# Revit family: Access_Door_ACUDOR_High-Security_SD-6000
name_source: partatom
category: Doors
revit_build: Autodesk Revit 2017 (Build: 20171027_0315(x64)
units: mm (PartAtom-declared; Revit-internal decimal feet)

## family parameters
Cut with Voids When Loaded = No
Host = Face
Room Calculation Point = No
Shared = No

## types (6) — shared parameters
Analytic Construction = <None>
Default Elevation = 48 "
Description = HIGH-SECURITY
Manufacturer = ACUDOR
Material Finish = Metal - Acudor - Stainless - Polished
URL = www.acudor.com
zero-valued in all types: Thickness, Wall Offset

## per-type parameters (varying)
| type | Code | Height | Width |
| SD-6000-1616 | 0 | 20 " | 20 " |
| SD-6000-1212 | 0 | 16 " | 16 " |
| SD-6000-1818 | 2 | 22 " | 22 " |
| SD-6000-2424 | 4 | 28 " | 28 " |
| SD-6000-2436 | 4 | 40 " | 28 " |
| SD-6000-3636 | 4 | 40 " | 40 " |

note: column(s) folded — value = type name in every type: Model

## geometry (parser evidence)
native form markers: Blend x2, Sweep x4
no freeform markers — native parametric forms only
